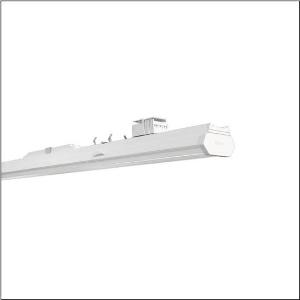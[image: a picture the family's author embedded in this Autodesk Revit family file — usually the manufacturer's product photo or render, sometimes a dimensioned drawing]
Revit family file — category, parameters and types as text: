
# Revit family: licross_11_protected_mo_51tp12dn595gd
name_source: partatom
category: Lighting Fixtures
units: mm (PartAtom-declared; Revit-internal decimal feet)

## family parameters
Cut with Voids When Loaded = No
Host = Face
Light Source = No
Part Type = Normal
Room Calculation Point = No
Round Connector Dimension = Use Diameter
Shared = No

## types (1)
- --- (1 x LED, 1580 lm, 9.9 W, 5000K)
    Apparent Load = 10 VA
    CIE Flux Codes = 73 92 98 99 100
    Color Rendering = 80
    Color Temperature = 5000K
    Default Elevation = 1800 mm
    Description = Licross 11 Protected MO, luminaire insert, of sheet steel, galvanised, coil coated, white, length: 1.500mm, width: 90mm, height: 101mm, LED rated luminous flux: 9.820lm, light colour: 850, SDCM (Standard Deviation of Colour Matching)MacAdam ≤ 2 SDCM (initial), control gear: DALI 2 (for two DALI lines), with plug, 6-pole, with phase selection, mains connection: 220..240V, AC/DC, 0/50..60Hz, rated input power: 57W, internal wiring halogen-free, for central battery installations according to EN 60598-2-22, for emergency light function, without changeover relay, primary optical cover: cover, of PMMA, light emission: direct distribution, primary light characteristic: symmetric, protection rating (complete): IP64, insulation class (complete): insulation class I (protective earthing), certification: CE, ENEC, VDE, UKCA, protection symbol: D if used in an environment without relevant dust loads with corresponding accessories, impact resistance: IK06, permissible ambient temperature for indoor applications: -25..+35°C, standard: EN 60598-2-22, corresponds to IFS (International Featured Standards) requirements for safety and quality in the food industry, reducing of maximum allowable ambient temperature of 5°C with ceiling mounting, LABS conformity tested according to VDMA 24364:2018-05, The light source and the operating device comply with the requirements of the Ecodesign Regulation (EU) 2019/2020 and are replaceable in accordance with this regulation, packaging unit: 1 piece
    Height = 92 mm
    Lamp = 1 x LED
    Lamp Light Flux = 1580 lm
    Lamp Power = 9.9 W
    Lamp count = 1
    Length = 1500 mm
    Luminous efficacy = 160 lm/W
    Manufacturer = Siteco
    ModVariant = No
    Model = 51TP12DN595GD
    Mounting Place = Ceiling
    Mounting Type = Pendant
    Number of Poles = 1
    OnlyDefault = Yes
    Power Factor = 1
    Product Name = Licross 11 Protected MO
    Product group = luminaire insert | ceiling pendant
    ProductGroupID = 901
    Protection Class = Protection class I
    Protection Degree = IP 64
    RLX_Detail_Level = 1
    RLX_Emergency_Light_Flux = 0 lm
    RLX_Emergency_Type = 0
    RLX_Emergency_Type_DB = No
    RlxData = <blob elided: 25129 chars, md5=ea3c8a5d>
    Socket = socket
    Standby Power = 0 W
    System Light Flux = 1580 lm
    System Power = 10 W
    Type Comments = : DC mode (central or group accumulator) initial emergency light level
    Type Image = l_1256148.jpg
    URL = http://relux.com
    VarID = @adj_038993
    Voltage = 0 V
    Weight = 0.00 kg
    Width = 88 mm

## geometry (parser evidence)
native form markers: Blend x4, Sweep x10
no freeform markers — native parametric forms only
